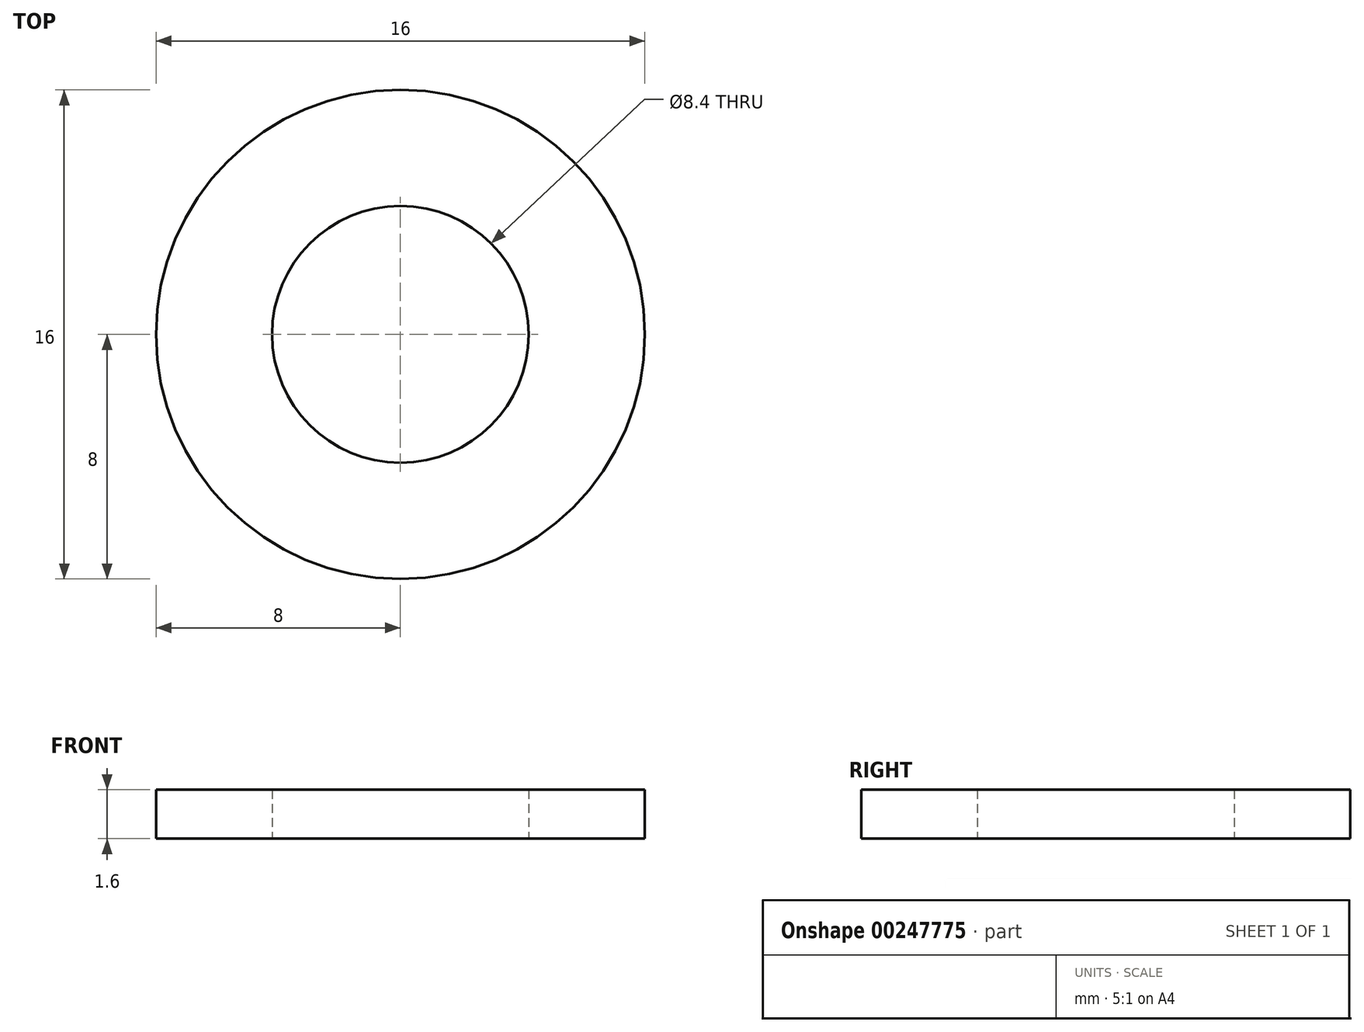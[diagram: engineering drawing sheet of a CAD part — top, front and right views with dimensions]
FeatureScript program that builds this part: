
annotation { "Feature Type Name" : "Feature", "Feature Type Description" : "" }
export const myFeature = defineFeature(function(context is Context, id is Id, definition is map)
    precondition{}
    {
        {
            var Q0;
            Q0=qCreatedBy(makeId("Top.planeOp"),FACE);
            var sketch = newSketch(context, id + "F0", { "sketchPlane" : qUnion([Q0])});
            skCircle(sketch, "E0", {"center": v(0, 0) * mm, "radius": 4.2 * mm});
            skCircle(sketch, "E1", {"center": v(0, 0) * mm, "radius": 8 * mm});
            skSolve(sketch);
        }
        {
            var Q0;
            Q0=qSketchRegion(id+"F0",true);
            extrude(context, id + "F1", {"entities" : qUnion([Q0]), "depth" : 1.6 * mm});
        }
    });
